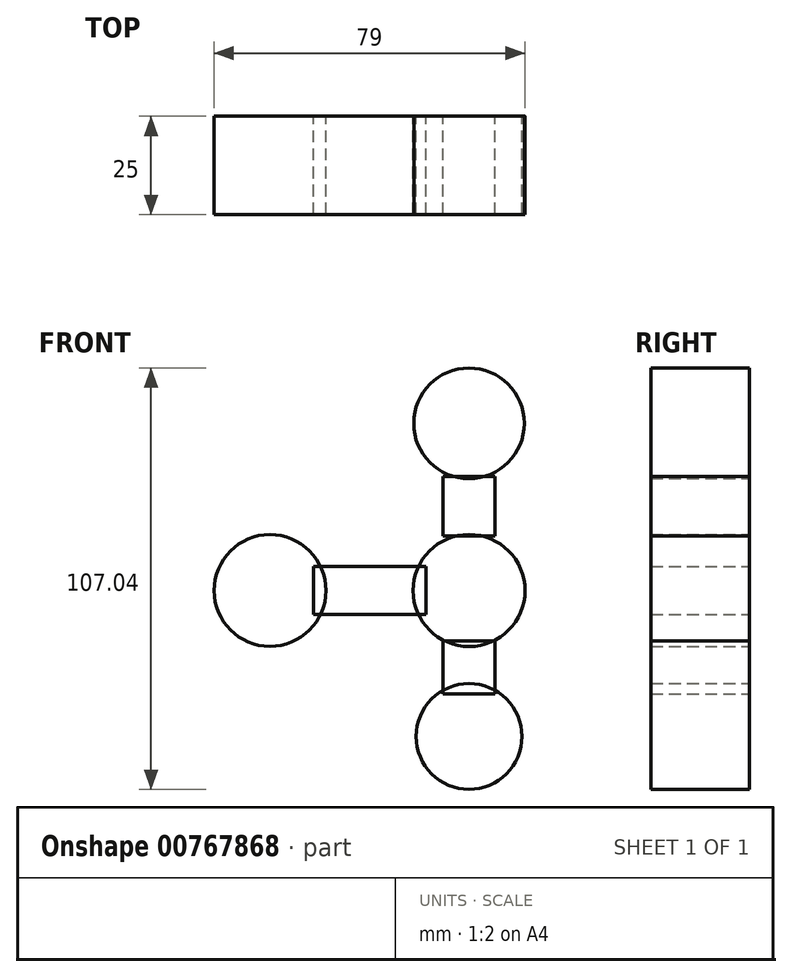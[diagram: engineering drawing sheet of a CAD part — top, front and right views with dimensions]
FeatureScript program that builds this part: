
annotation { "Feature Type Name" : "Feature", "Feature Type Description" : "" }
export const myFeature = defineFeature(function(context is Context, id is Id, definition is map)
    precondition{}
    {
        {
            var Q0;
            Q0=qCreatedBy(makeId("Front.planeOp"),FACE);
            var sketch = newSketch(context, id + "F0", { "sketchPlane" : qUnion([Q0])});
            skCircle(sketch, "E0", {"center": v(0, 0) * mm, "radius": 14.22 * mm});
            skSolve(sketch);
        }
        {
            var Q0;
            Q0 = qSketchRegion(id + "F0", true);
            extrude(context, id + "F1", {"entities" : qUnion([Q0]), "depth" : 25 * mm, "offsetDistance" : 25.4 * mm});
        }
        {
            var Q0;
            Q0=qCreatedBy(makeId("Front.planeOp"),FACE);
            var sketch = newSketch(context, id + "F2", { "sketchPlane" : qUnion([Q0])});
            skCircle(sketch, "E1", {"center": v(0, 42.48) * mm, "radius": 14.04 * mm});
            skSolve(sketch);
        }
        {
            var Q0;
            Q0 = qSketchRegion(id + "F2", true);
            extrude(context, id + "F3", {"entities" : qUnion([Q0]), "depth" : 25 * mm, "offsetDistance" : 25 * mm});
        }
        {
            var Q0;
            Q0=qCreatedBy(makeId("Front.planeOp"),FACE);
            var sketch = newSketch(context, id + "F4", { "sketchPlane" : qUnion([Q0])});
            skCircle(sketch, "E2", {"center": v(0, -37.08) * mm, "radius": 13.43 * mm});
            skSolve(sketch);
        }
        {
            var Q0;
            Q0 = qSketchRegion(id + "F4", true);
            extrude(context, id + "F5", {"entities" : qUnion([Q0]), "depth" : 25 * mm, "offsetDistance" : 25 * mm});
        }
        {
            var Q0;
            Q0=qCreatedBy(makeId("Front.planeOp"),FACE);
            var sketch = newSketch(context, id + "F6", { "sketchPlane" : qUnion([Q0])});
            skCircle(sketch, "E3", {"center": v(-50.57, 0) * mm, "radius": 14.21 * mm});
            skSolve(sketch);
        }
        {
            var Q0;
            Q0 = qSketchRegion(id + "F6", true);
            extrude(context, id + "F7", {"entities" : qUnion([Q0]), "depth" : 25 * mm, "offsetDistance" : 25 * mm});
        }
        {
            var Q0;
            Q0=qCreatedBy(makeId("Front.planeOp"),FACE);
            var sketch = newSketch(context, id + "F8", { "sketchPlane" : qUnion([Q0])});
            skLineSegment(sketch, "E4.bottom", {"start": v(6.6, 29) * mm, "end": v(-6.6, 29) * mm});
            skLineSegment(sketch, "E4.top", {"start": v(6.6, 13.89) * mm, "end": v(-6.6, 13.89) * mm});
            skLineSegment(sketch, "E4.left", {"start": v(6.6, 29) * mm, "end": v(6.6, 13.89) * mm});
            skLineSegment(sketch, "E4.right", {"start": v(-6.6, 29) * mm, "end": v(-6.6, 13.89) * mm});
            skPoint(sketch, "E4.middle", {"position": v(0, 21.44) * mm});
            skLineSegment(sketch, "E5.bottom", {"start": v(6.6, -12.81) * mm, "end": v(-6.6, -12.81) * mm});
            skLineSegment(sketch, "E5.top", {"start": v(6.6, -26.3) * mm, "end": v(-6.6, -26.3) * mm});
            skLineSegment(sketch, "E5.left", {"start": v(6.6, -12.81) * mm, "end": v(6.6, -26.3) * mm});
            skLineSegment(sketch, "E5.right", {"start": v(-6.6, -12.81) * mm, "end": v(-6.6, -26.3) * mm});
            skPoint(sketch, "E5.middle", {"position": v(0, -19.55) * mm});
            skLineSegment(sketch, "E6.bottom", {"start": v(-10.92, 6.07) * mm, "end": v(-39.5, 6.07) * mm});
            skLineSegment(sketch, "E6.top", {"start": v(-10.92, -6.07) * mm, "end": v(-39.5, -6.07) * mm});
            skLineSegment(sketch, "E6.left", {"start": v(-10.92, 6.07) * mm, "end": v(-10.92, -6.07) * mm});
            skLineSegment(sketch, "E6.right", {"start": v(-39.5, 6.07) * mm, "end": v(-39.5, -6.07) * mm});
            skPoint(sketch, "E6.middle", {"position": v(-25.22, 0) * mm});
            skSolve(sketch);
        }
        {
            var Q0;
            Q0 = qSketchRegion(id + "F8", true);
            extrude(context, id + "F9", {"entities" : qUnion([Q0]), "depth" : 25 * mm, "offsetDistance" : 25 * mm});
        }
    });
